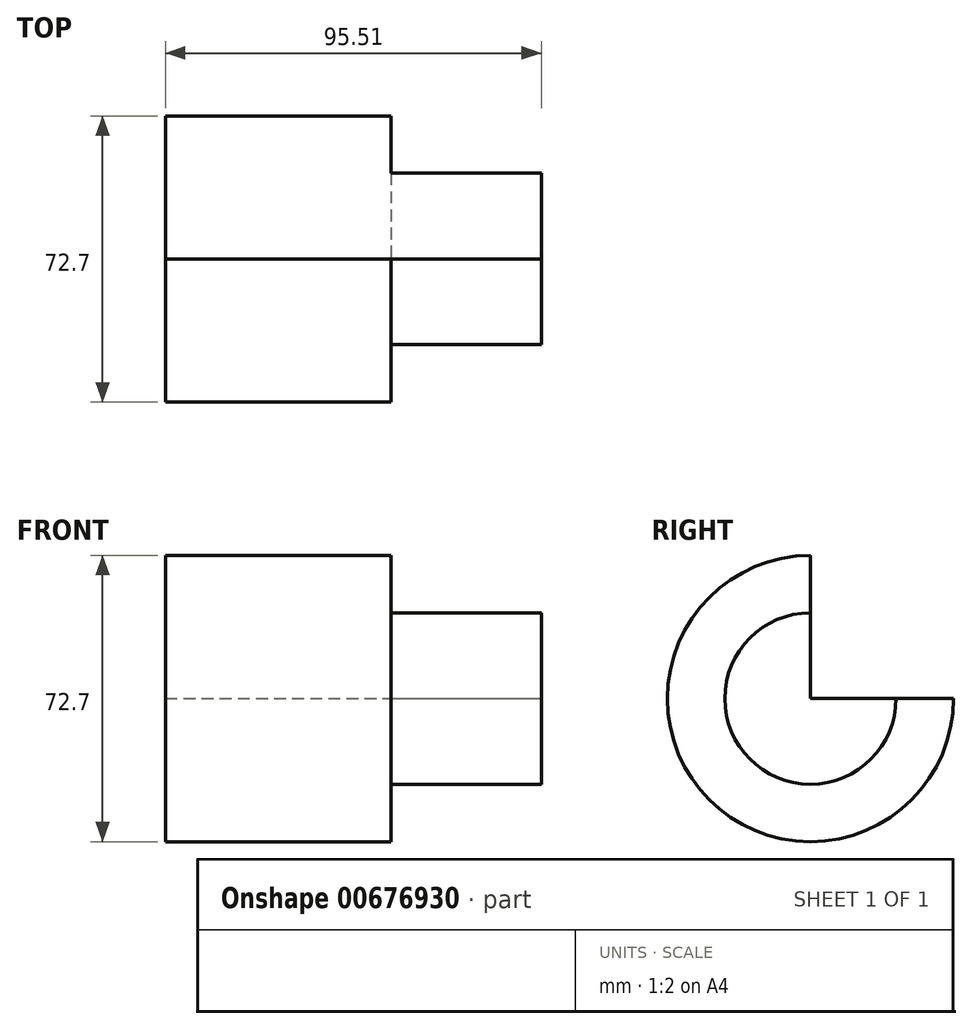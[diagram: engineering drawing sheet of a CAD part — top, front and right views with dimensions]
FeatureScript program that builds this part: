
annotation { "Feature Type Name" : "Feature", "Feature Type Description" : "" }
export const myFeature = defineFeature(function(context is Context, id is Id, definition is map)
    precondition{}
    {
        {
            var Q0;
            Q0=qCreatedBy(makeId("Front.planeOp"),FACE);
            var sketch = newSketch(context, id + "F0", { "sketchPlane" : qUnion([Q0])});
            skLineSegment(sketch, "E0.bottom", {"start": v(0, 0) * mm, "end": v(57.36, 0) * mm});
            skLineSegment(sketch, "E0.top", {"start": v(0, 36.35) * mm, "end": v(57.36, 36.35) * mm});
            skLineSegment(sketch, "E0.left", {"start": v(0, 0) * mm, "end": v(0, 36.35) * mm});
            skLineSegment(sketch, "E0.right", {"start": v(57.36, 0) * mm, "end": v(57.36, 36.35) * mm});
            skLineSegment(sketch, "E1.bottom", {"start": v(57.36, 0) * mm, "end": v(95.5, 0) * mm});
            skLineSegment(sketch, "E1.top", {"start": v(57.36, 21.75) * mm, "end": v(95.5, 21.75) * mm});
            skLineSegment(sketch, "E1.left", {"start": v(57.36, 0) * mm, "end": v(57.36, 21.75) * mm});
            skLineSegment(sketch, "E1.right", {"start": v(95.5, 0) * mm, "end": v(95.5, 21.75) * mm});
            skSolve(sketch);
        }
        {
            var Q0;
            Q0=makeQuery(id+"F0.imprint","IMPRINT",FACE,{"disambiguationData":[TD([[makeQuery(id+"F0.imprint","IMPRINT",EDGE,{"derivedFrom":sQuery(id+"F0.wireOp",EDGE,"E0.bottom")}),1.0]])]});
            var Q1;
            Q1=makeQuery(id+"F0.imprint","IMPRINT",FACE,{"disambiguationData":[TD([[makeQuery(id+"F0.imprint","IMPRINT",EDGE,{"derivedFrom":sQuery(id+"F0.wireOp",EDGE,"E1.bottom")}),1.0]])]});
            var Q2;
            Q2=sQuery(id+"F0.wireOp",EDGE,"E0.bottom");
            revolve(context, id + "F1", {"entities" : qUnion([Q0, Q1]), "axis" : qUnion([Q2]), "revolveType" : RevolveType.ONE_DIRECTION, "angle" : 270 * degree});
        }
    });
